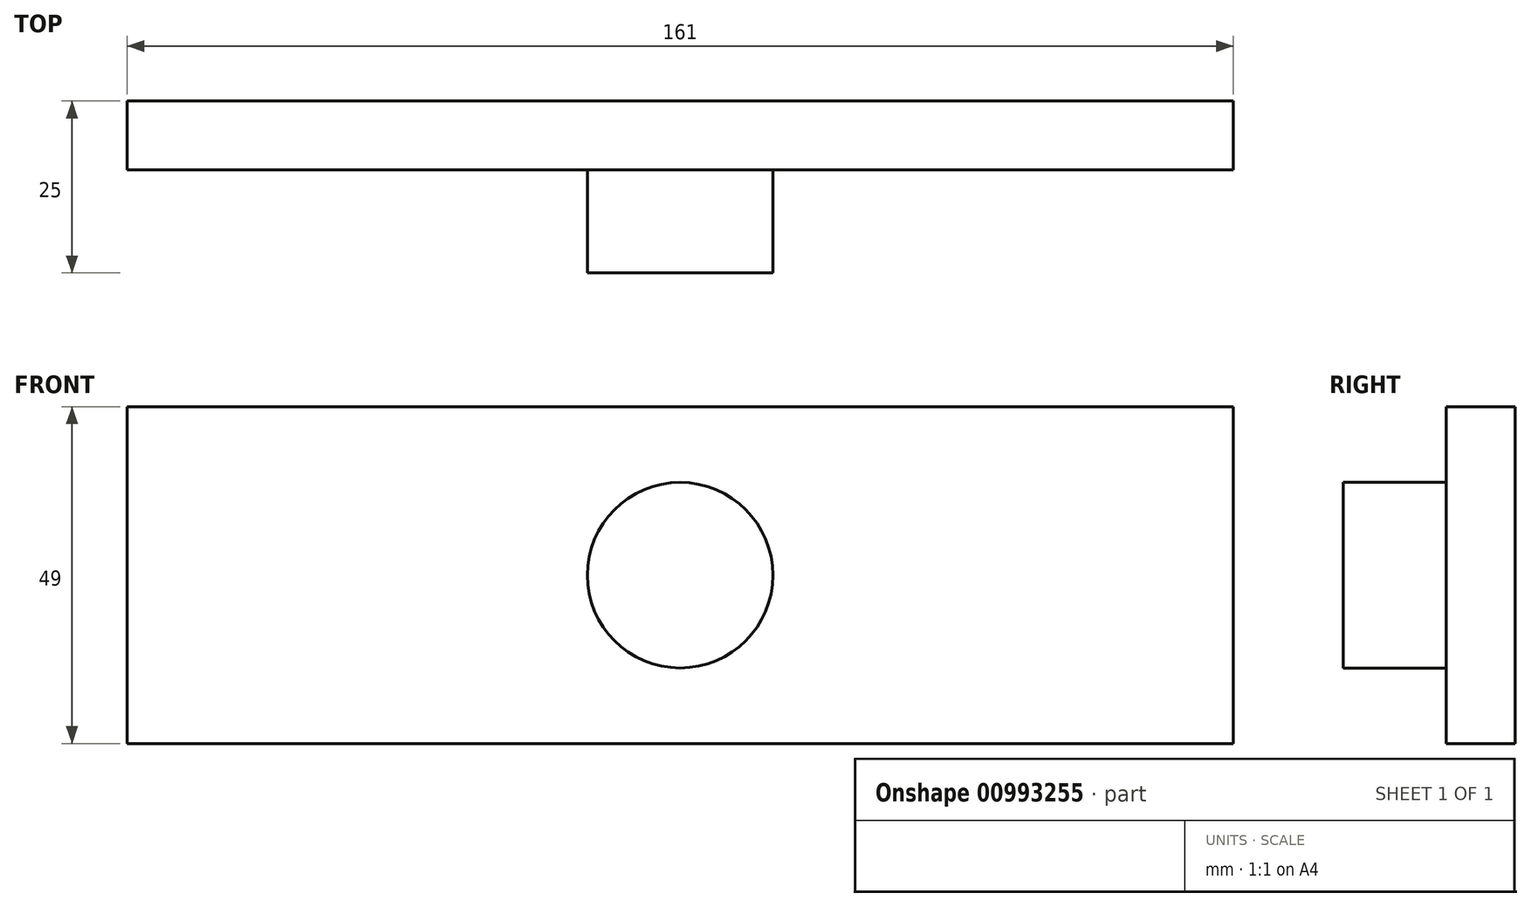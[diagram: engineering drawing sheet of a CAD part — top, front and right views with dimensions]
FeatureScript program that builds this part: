
annotation { "Feature Type Name" : "Feature", "Feature Type Description" : "" }
export const myFeature = defineFeature(function(context is Context, id is Id, definition is map)
    precondition{}
    {
        {
            var Q0;
            Q0=qCreatedBy(makeId("Front.planeOp"),FACE);
            var sketch = newSketch(context, id + "F0", { "sketchPlane" : qUnion([Q0])});
            skCircle(sketch, "E0", {"center": v(0, 0) * mm, "radius": 13.5 * mm});
            skLineSegment(sketch, "E1.bottom", {"start": v(80.5, -24.5) * mm, "end": v(-80.5, -24.5) * mm});
            skLineSegment(sketch, "E1.top", {"start": v(80.5, 24.5) * mm, "end": v(-80.5, 24.5) * mm});
            skLineSegment(sketch, "E1.left", {"start": v(80.5, -24.5) * mm, "end": v(80.5, 24.5) * mm});
            skLineSegment(sketch, "E1.right", {"start": v(-80.5, -24.5) * mm, "end": v(-80.5, 24.5) * mm});
            skSolve(sketch);
        }
        {
            var Q0;
            Q0=makeQuery(id+"F0.imprint","IMPRINT",FACE,{"disambiguationData":[TD([[makeQuery(id+"F0.imprint","IMPRINT",EDGE,{"derivedFrom":sQuery(id+"F0.wireOp",EDGE,"E0")}),1.0]])]});
            extrude(context, id + "F1", {"entities" : qUnion([Q0]), "depth" : 25 * mm, "offsetDistance" : 25 * mm});
        }
        {
            var Q0;
            Q0 = qSketchRegion(id + "F0", true);
            extrude(context, id + "F2", {"entities" : qUnion([Q0]), "operationType" : NewBodyOperationType.ADD, "depth" : 10 * mm, "offsetDistance" : 25 * mm});
        }
    });
